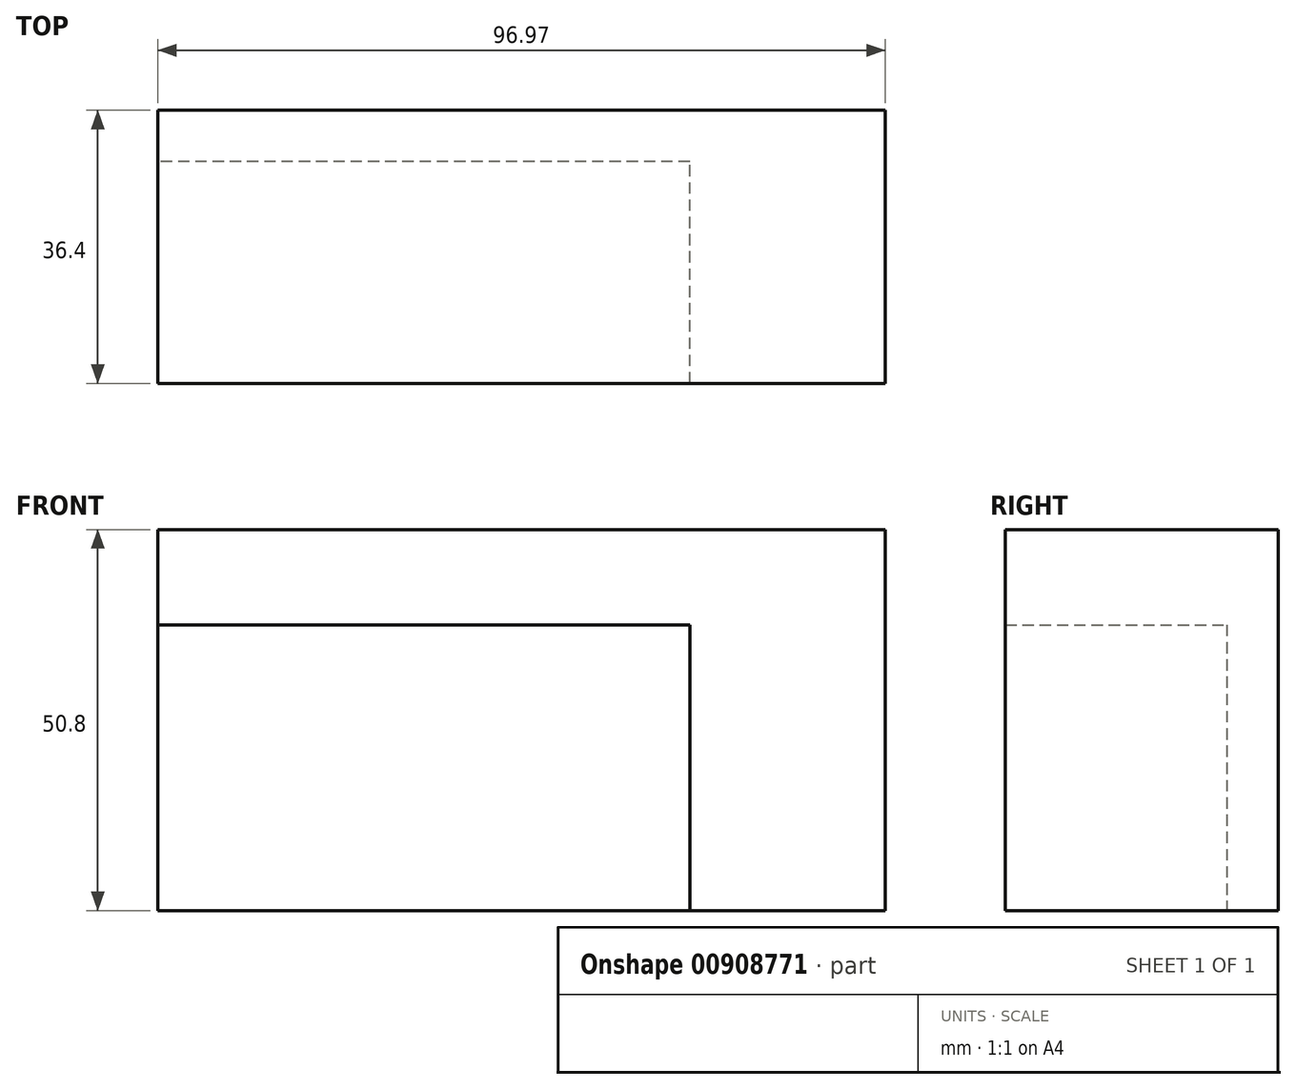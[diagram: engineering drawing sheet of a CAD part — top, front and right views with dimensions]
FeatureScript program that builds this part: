
annotation { "Feature Type Name" : "Feature", "Feature Type Description" : "" }
export const myFeature = defineFeature(function(context is Context, id is Id, definition is map)
    precondition{}
    {
        {
            var Q0;
            Q0=qCreatedBy(makeId("Top.planeOp"),FACE);
            var sketch = newSketch(context, id + "F0", { "sketchPlane" : qUnion([Q0])});
            skLineSegment(sketch, "E0.bottom", {"start": v(-73.16, 33.72) * mm, "end": v(71.07, 33.72) * mm});
            skLineSegment(sketch, "E0.top", {"start": v(-73.16, -48.05) * mm, "end": v(71.07, -48.05) * mm});
            skLineSegment(sketch, "E0.left", {"start": v(-73.16, 33.72) * mm, "end": v(-73.16, -48.05) * mm});
            skLineSegment(sketch, "E0.right", {"start": v(71.07, 33.72) * mm, "end": v(71.07, -48.05) * mm});
            skSolve(sketch);
        }
        {
            var Q0;
            Q0 = qSketchRegion(id + "F0", true);
            extrude(context, id + "F1", {"entities" : qUnion([Q0]), "depth" : 25.4 * mm, "offsetDistance" : 25.4 * mm});
        }
        {
            var Q0;
            Q0=qCreatedBy(makeId("Top.planeOp"),FACE);
            var sketch = newSketch(context, id + "F2", { "sketchPlane" : qUnion([Q0])});
            skLineSegment(sketch, "E1.bottom", {"start": v(109.83, 16.86) * mm, "end": v(12.86, 16.86) * mm});
            skLineSegment(sketch, "E1.top", {"start": v(109.83, 53.26) * mm, "end": v(12.86, 53.26) * mm});
            skLineSegment(sketch, "E1.left", {"start": v(109.83, 16.86) * mm, "end": v(109.83, 53.26) * mm});
            skLineSegment(sketch, "E1.right", {"start": v(12.86, 16.86) * mm, "end": v(12.86, 53.26) * mm});
            skSolve(sketch);
        }
        {
            var Q0;
            Q0 = qSketchRegion(id + "F2", true);
            extrude(context, id + "F3", {"entities" : qUnion([Q0]), "depth" : 50.8 * mm, "offsetDistance" : 25.4 * mm});
        }
        {
            var Q0;
            Q0=makeQuery(id+"F1.opExtrude","SWEPT_BODY",BODY,{"disambiguationData":[OSD([sQuery(id+"F0.wireOp",EDGE,"E0.bottom"),sQuery(id+"F0.wireOp",EDGE,"E0.top"),sQuery(id+"F0.wireOp",EDGE,"E0.left"),sQuery(id+"F0.wireOp",EDGE,"E0.right")])]});
            var Q1;
            Q1=makeQuery(id+"F3.opExtrude","SWEPT_BODY",BODY,{"disambiguationData":[OSD([sQuery(id+"F2.wireOp",EDGE,"E1.bottom"),sQuery(id+"F2.wireOp",EDGE,"E1.top"),sQuery(id+"F2.wireOp",EDGE,"E1.left"),sQuery(id+"F2.wireOp",EDGE,"E1.right")])]});
            booleanBodies(context, id + "F4", {"operationType" : BooleanOperationType.SUBTRACTION, "tools" : qUnion([Q0]), "targets" : qUnion([Q1]), "offset" : true, "offsetAll" : true, "offsetDistance" : 12.7 * mm});
        }
    });
